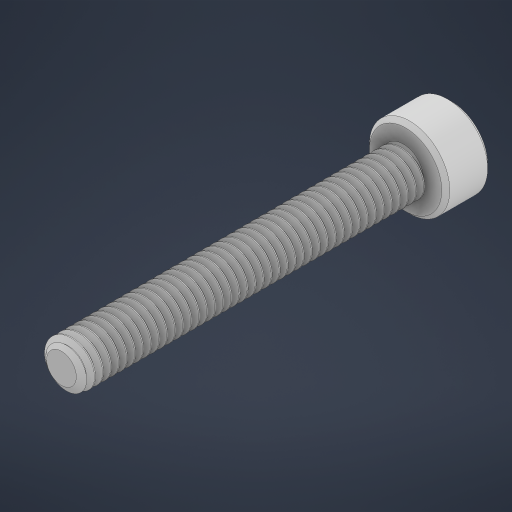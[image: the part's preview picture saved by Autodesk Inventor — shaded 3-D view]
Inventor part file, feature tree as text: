
AUTODESK INVENTOR PART (.ipt)
format: ipt  version: 2023 (Build 270158000, 158)  size: 1,321,472 bytes
history: native  units: in
note: dims shown in document units (in); Inventor stores cm internally (conversion verified against a paired STEP export)
features: chamfer x1
ambient origin geometry x8: Origin, YZ Plane, XZ Plane, XY Plane, X Axis, Y Axis, Z Axis, Center Point
bodies: Solid1 (feature_tree)
feature tree (1):
  chamfer  "Chamfer1"  [1 undecoded]
note: 1 required parameter value undecoded (feature->parameter linkage not recoverable at this tier; creation-order binding heuristic only, values carry confidence <= 0.55)
